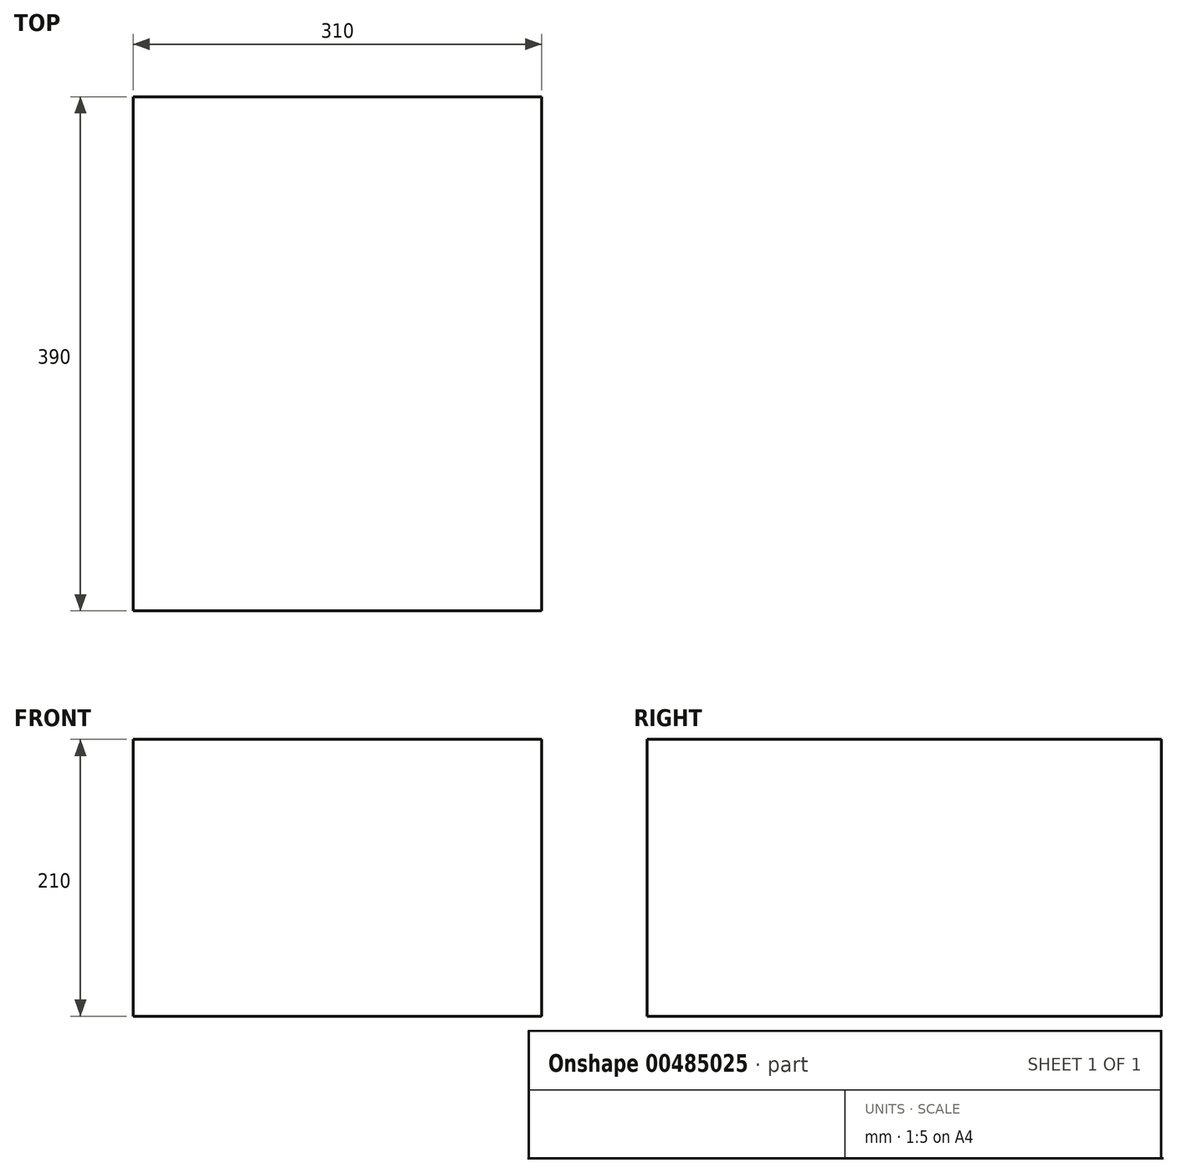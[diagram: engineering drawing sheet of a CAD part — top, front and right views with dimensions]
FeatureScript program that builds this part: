
annotation { "Feature Type Name" : "Feature", "Feature Type Description" : "" }
export const myFeature = defineFeature(function(context is Context, id is Id, definition is map)
    precondition{}
    {
        {
            var Q0;
            Q0=qCreatedBy(makeId("Top.planeOp"),FACE);
            var sketch = newSketch(context, id + "F0", { "sketchPlane" : qUnion([Q0])});
            skLineSegment(sketch, "E0.bottom", {"start": v(155, -195) * mm, "end": v(-155, -195) * mm});
            skLineSegment(sketch, "E0.top", {"start": v(155, 195) * mm, "end": v(-155, 195) * mm});
            skLineSegment(sketch, "E0.left", {"start": v(155, -195) * mm, "end": v(155, 195) * mm});
            skLineSegment(sketch, "E0.right", {"start": v(-155, -195) * mm, "end": v(-155, 195) * mm});
            skPoint(sketch, "E0.middle", {"position": v(0, 0) * mm});
            skSolve(sketch);
        }
        {
            var Q0;
            Q0 = qSketchRegion(id + "F0", true);
            extrude(context, id + "F1", {"entities" : qUnion([Q0]), "depth" : 210 * mm, "offsetDistance" : 25 * mm});
        }
    });
